# Revit family: 0047996
name_source: partatom
category: Lighting Fixtures
revit_build: Autodesk Revit 2016 (Build: 20150220_1215(x64)
units: mm (PartAtom-declared; Revit-internal decimal feet)

## family parameters
Cut with Voids When Loaded = No
Host = Face
Light Source = Yes
OmniClass Number = 23.80.70.00
OmniClass Title = Lighting
Part Type = Normal
Room Calculation Point = No
Round Connector Dimension = Use Diameter
Shared = No

## types (8) — shared parameters
Assembly Code = D5020200
AssetType = Fixed
BezelOffset_SYL = 30 mm
ClassificationName = Uniclass2015
ClassificationValue = EF_70_80
Color Filter = 16777215
Default Elevation = 1219 mm
DiffuserWidth_SYL = 546 mm  [stored 1.79134 ft]
Dimming Lamp Color Temperature Shift = <None>
DocumentationLiterature = http://www.sylvania-lighting.com
DurationUnit = hours
ElectricShockClassification = Class II
Emit Shape Visible in Rendering = No
Emit from Rectangle Length = 566 mm
Emit from Rectangle Width = 566 mm
ExpectedLife = 50000
IfcExportAs = IfcLightFixtureType
IfcExportType = IfcLightFixtureType
ImpactProtectionIndex = IK03
IngressProtection = IP44/20
Keynote = 16500
Lamp = LED
LampColourRenderingIndex = 80
LampColourTemperature = 3000 K
LampsType = LED
Length_SYL = 596 mm  [stored 1.95538 ft]
Manufacturer = Feilo Sylvania
ManufacturerName = Feilo Sylvania
Material = steel housing, pc diffuser
Material_1_SYL = Body-Sylvania-Start Panel LED DALI-White
Material_2_SYL = Diffuser-Sylvania-Start Panel LED DALI
Material_3_SYL = <By Category>
Material_4_SYL = <By Category>
Model = S Panel UGR19 625x625 IP44 Mltpwr 1500-4350Lm 830
ModelNumber = 0047996
ModelReference = S Panel UGR19 625x625 IP44 Mltpwr 1500-4350Lm 830
Name = S Panel UGR19 625x625 IP44 Mltpwr 1500-4350Lm 830
NominalDepth = 620 mm  [stored 2.03412 ft]
NominalHeight = 65 mm  [stored 0.213255 ft]
NominalLength = 620 mm  [stored 2.03412 ft]
PowerFactor = 0.95
Tilt Angle = -90.00°
Type Image = <None>
TypeName = S Panel UGR19 625x625 IP44 Mltpwr 1500-4350Lm 830
URL = http://www.sylvania-lighting.com
Voltage = 0 V
zero-valued in all types: Cost

## per-type parameters (varying)
| type | Apparent Load | LampNominalLuminous | LuminousEfficacy | Photometric Web File | PowerConsumption |
| 0047996 36W | 36 VA | 4422 lm | 122.5 lm/W | 0047996_36W.ies | 36 W |
| 0047996 32W | 32 VA | 3951 lm | 123.8 lm/W | 0047996_32W.ies | 32 W |
| 0047996 29W | 29 VA | 3584 lm | 124.4 lm/W | 0047996_29W.ies | 29 W |
| 0047996 25W | 25 VA | 3111 lm | 125.9 lm/W | 0047996_25W.ies | 25 W |
| 0047996 23W | 23 VA | 2923 lm | 126.0 lm/W | 0047996_23W.ies | 23 W |
| 0047996 19W | 19 VA | 2013 lm | 104.8 lm/W | 0047996_19W.ies | 19 W |
| 0047996 16W | 16 VA | 2024 lm | 124.9 lm/W | 0047996_16W.ies | 16 W |
| 0047996 13W | 13 VA | 1536 lm | 121.9 lm/W | 0047996_13W.ies | 13 W |

note: [stored X ft] marks values corroborated as IEEE doubles in the binary element streams (Revit-internal decimal feet)

## geometry (parser evidence)
native form markers: Sweep x1
no freeform markers — native parametric forms only
